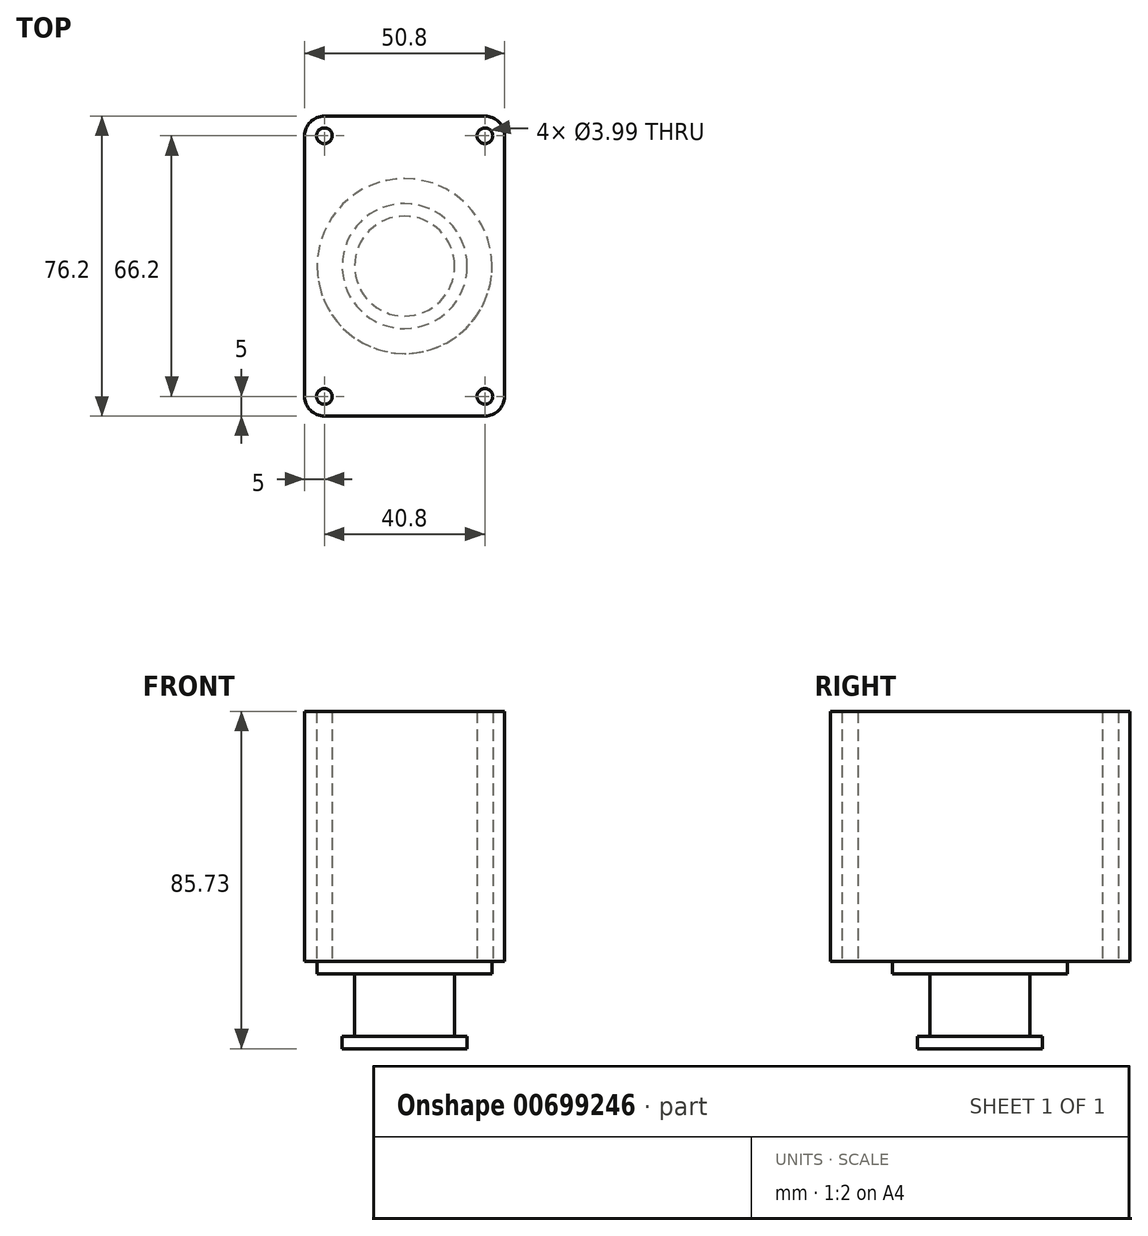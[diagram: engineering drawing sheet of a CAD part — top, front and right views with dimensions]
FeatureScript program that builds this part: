
annotation { "Feature Type Name" : "Feature", "Feature Type Description" : "" }
export const myFeature = defineFeature(function(context is Context, id is Id, definition is map)
    precondition{}
    {
        {
            var Q0;
            Q0=qCreatedBy(makeId("Top.planeOp"),FACE);
            var sketch = newSketch(context, id + "F0", { "sketchPlane" : qUnion([Q0])});
            skLineSegment(sketch, "E0.bottom", {"start": v(-20.4, -38.1) * mm, "end": v(20.4, -38.1) * mm});
            skLineSegment(sketch, "E0.top", {"start": v(-20.4, 38.1) * mm, "end": v(20.4, 38.1) * mm});
            skLineSegment(sketch, "E0.left", {"start": v(-25.4, -33.1) * mm, "end": v(-25.4, 33.1) * mm});
            skLineSegment(sketch, "E0.right", {"start": v(25.4, -33.1) * mm, "end": v(25.4, 33.1) * mm});
            skPoint(sketch, "E1.visualSharp", {"position": v(-25.4, -38.1) * mm});
            skArc(sketch, "E1.filletArc", {"start": v(-25.4, -33.1) * mm, "mid": v(-23.94, -36.64) * mm, "end": v(-20.4, -38.1) * mm});
            skPoint(sketch, "E2.visualSharp", {"position": v(-25.4, 38.1) * mm});
            skArc(sketch, "E2.filletArc", {"start": v(-20.4, 38.1) * mm, "mid": v(-23.94, 36.64) * mm, "end": v(-25.4, 33.1) * mm});
            skPoint(sketch, "E3.visualSharp", {"position": v(25.4, 38.1) * mm});
            skArc(sketch, "E3.filletArc", {"start": v(25.4, 33.1) * mm, "mid": v(23.94, 36.64) * mm, "end": v(20.4, 38.1) * mm});
            skPoint(sketch, "E4.visualSharp", {"position": v(25.4, -38.1) * mm});
            skArc(sketch, "E4.filletArc", {"start": v(20.4, -38.1) * mm, "mid": v(23.94, -36.64) * mm, "end": v(25.4, -33.1) * mm});
            skCircle(sketch, "E5", {"center": v(-20.4, -33.1) * mm, "radius": 2 * mm});
            skCircle(sketch, "E6.MirrorC", {"center": v(20.4, -33.1) * mm, "radius": 2 * mm});
            skCircle(sketch, "E7.MirrorC", {"center": v(-20.4, 33.1) * mm, "radius": 2 * mm});
            skCircle(sketch, "E8.MirrorC", {"center": v(20.4, 33.1) * mm, "radius": 2 * mm});
            skSolve(sketch);
        }
        {
            var Q0;
            Q0=qSketchRegion(id+"F0",true);
            extrude(context, id + "F1", {"entities" : qUnion([Q0]), "depth" : 63.5 * mm, "offsetDistance" : 25 * mm});
        }
        {
            var Q0;
            Q0=makeQuery(id+"F1.opExtrude","CAP_FACE",FACE,{"disambiguationData":[OSD([sQuery(id+"F0.wireOp",EDGE,"E0.bottom"),sQuery(id+"F0.wireOp",EDGE,"E0.top"),sQuery(id+"F0.wireOp",EDGE,"E0.left"),sQuery(id+"F0.wireOp",EDGE,"E0.right"),sQuery(id+"F0.wireOp",EDGE,"E1.filletArc"),sQuery(id+"F0.wireOp",EDGE,"E2.filletArc"),sQuery(id+"F0.wireOp",EDGE,"E3.filletArc"),sQuery(id+"F0.wireOp",EDGE,"E4.filletArc"),sQuery(id+"F0.wireOp",EDGE,"E5"),sQuery(id+"F0.wireOp",EDGE,"E6.MirrorC"),sQuery(id+"F0.wireOp",EDGE,"E7.MirrorC"),sQuery(id+"F0.wireOp",EDGE,"E8.MirrorC")])],"isStart":true});
            var sketch = newSketch(context, id + "F2", { "sketchPlane" : qUnion([Q0])});
            skCircle(sketch, "E9", {"center": v(0, 0) * mm, "radius": 12.7 * mm});
            skSolve(sketch);
        }
        {
            var Q0;
            Q0=makeQuery(id+"F2.imprint","IMPRINT",FACE,{"disambiguationData":[TD([[makeQuery(id+"F2.imprint","IMPRINT",EDGE,{"derivedFrom":sQuery(id+"F2.wireOp",EDGE,"E9")}),1.0]])]});
            var Q1;
            Q1=sQuery(id+"F2.wireOp",EDGE,"E9");
            extrude(context, id + "F3", {"entities" : qUnion([Q0]), "operationType" : NewBodyOperationType.ADD, "surfaceEntities" : qUnion([Q1]), "depth" : 19.05 * mm, "offsetDistance" : 25.4 * mm});
        }
        {
            var Q0;
            Q0=makeQuery(id+"F1.opExtrude","CAP_FACE",FACE,{"disambiguationData":[OSD([sQuery(id+"F0.wireOp",EDGE,"E0.bottom"),sQuery(id+"F0.wireOp",EDGE,"E0.top"),sQuery(id+"F0.wireOp",EDGE,"E0.left"),sQuery(id+"F0.wireOp",EDGE,"E0.right"),sQuery(id+"F0.wireOp",EDGE,"E1.filletArc"),sQuery(id+"F0.wireOp",EDGE,"E2.filletArc"),sQuery(id+"F0.wireOp",EDGE,"E3.filletArc"),sQuery(id+"F0.wireOp",EDGE,"E4.filletArc"),sQuery(id+"F0.wireOp",EDGE,"E5"),sQuery(id+"F0.wireOp",EDGE,"E6.MirrorC"),sQuery(id+"F0.wireOp",EDGE,"E7.MirrorC"),sQuery(id+"F0.wireOp",EDGE,"E8.MirrorC")])],"isStart":true});
            var sketch = newSketch(context, id + "F4", { "sketchPlane" : qUnion([Q0])});
            skCircle(sketch, "E10", {"center": v(0, 0) * mm, "radius": 22.23 * mm});
            skSolve(sketch);
        }
        {
            var Q0;
            Q0=makeQuery(id+"F4.imprint","IMPRINT",FACE,{"disambiguationData":[TD([[makeQuery(id+"F4.imprint","IMPRINT",EDGE,{"derivedFrom":sQuery(id+"F4.wireOp",EDGE,"E10")}),1.0]])]});
            extrude(context, id + "F5", {"entities" : qUnion([Q0]), "operationType" : NewBodyOperationType.ADD, "depth" : 3.17 * mm, "offsetDistance" : 25.4 * mm});
        }
        {
            var Q0;
            Q0=makeQuery(id+"F3.opExtrude","CAP_FACE",FACE,{"disambiguationData":[OSD([sQuery(id+"F2.wireOp",EDGE,"E9")])],"isStart":false});
            var sketch = newSketch(context, id + "F6", { "sketchPlane" : qUnion([Q0])});
            skCircle(sketch, "E11", {"center": v(0, 0) * mm, "radius": 15.88 * mm});
            skSolve(sketch);
        }
        {
            var Q0;
            Q0 = qSketchRegion(id + "F6", true);
            extrude(context, id + "F7", {"entities" : qUnion([Q0]), "operationType" : NewBodyOperationType.ADD, "depth" : 3.17 * mm, "offsetDistance" : 25.4 * mm});
        }
    });
